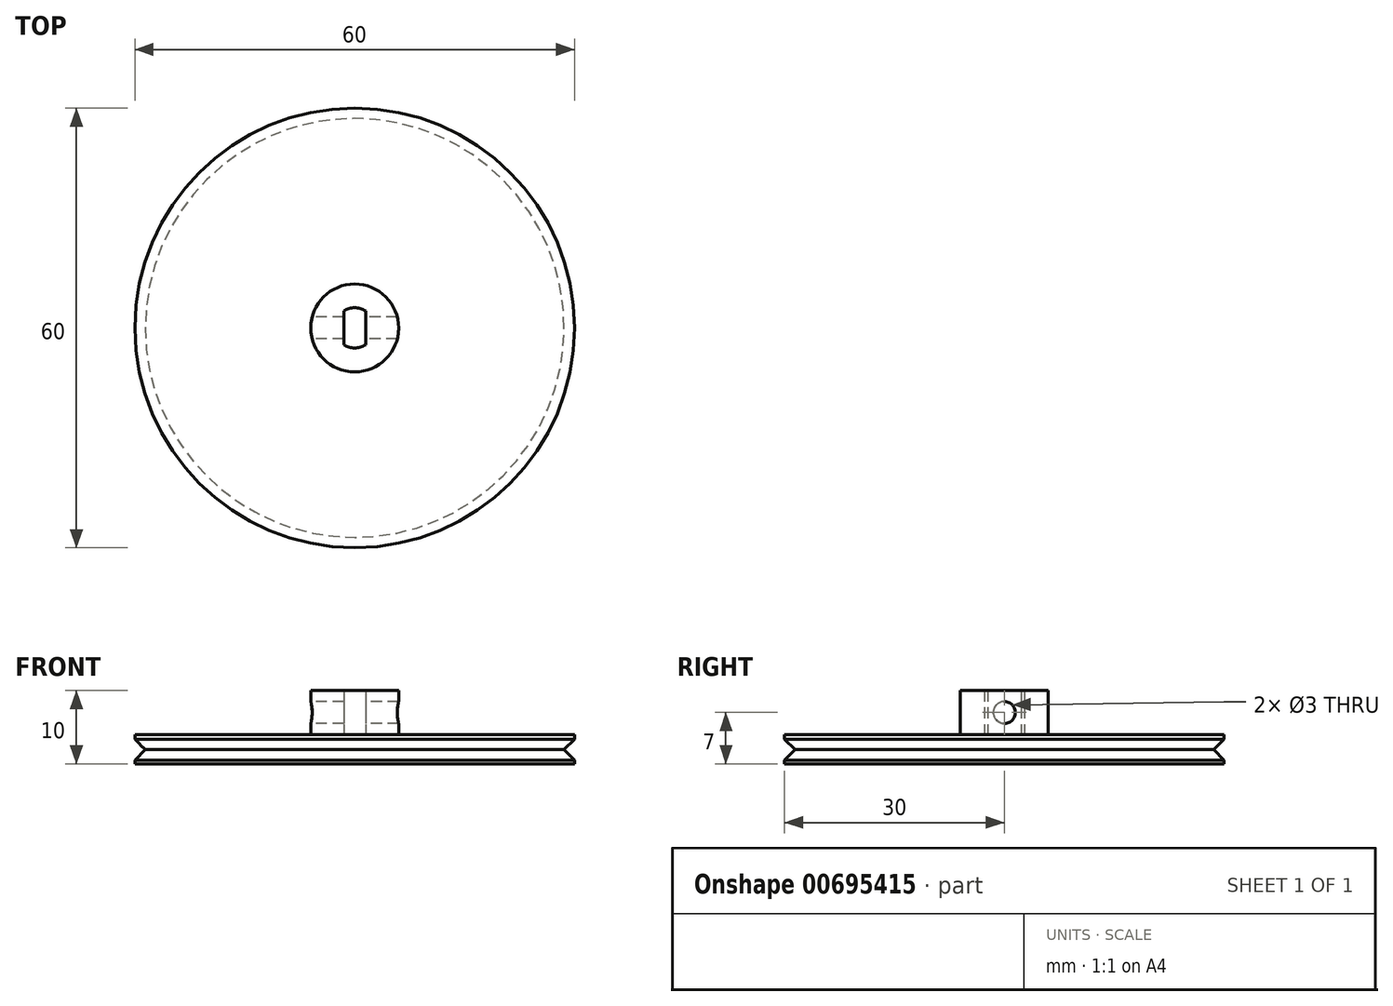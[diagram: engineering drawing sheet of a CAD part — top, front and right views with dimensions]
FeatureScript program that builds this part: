
annotation { "Feature Type Name" : "Feature", "Feature Type Description" : "" }
export const myFeature = defineFeature(function(context is Context, id is Id, definition is map)
    precondition{}
    {
        {
            var Q0;
            Q0=qCreatedBy(makeId("Top.planeOp"),FACE);
            var sketch = newSketch(context, id + "F0", { "sketchPlane" : qUnion([Q0])});
            skCircle(sketch, "E0", {"center": v(0, 0) * mm, "radius": 30 * mm});
            skSolve(sketch);
        }
        {
            var Q0;
            Q0=makeQuery(id+"F0.imprint","IMPRINT",FACE,{"disambiguationData":[TD([[makeQuery(id+"F0.imprint","IMPRINT",EDGE,{"derivedFrom":sQuery(id+"F0.wireOp",EDGE,"E0")}),1.0]])]});
            extrude(context, id + "F1", {"entities" : qUnion([Q0]), "depth" : 4 * mm, "offsetDistance" : 25 * mm});
        }
        {
            var Q0;
            Q0=makeQuery(id+"F1.opExtrude","CAP_FACE",FACE,{"disambiguationData":[OSD([sQuery(id+"F0.wireOp",EDGE,"E0")])],"isStart":false});
            var sketch = newSketch(context, id + "F2", { "sketchPlane" : qUnion([Q0])});
            skCircle(sketch, "E1", {"center": v(0, 0) * mm, "radius": 6 * mm});
            skLineSegment(sketch, "E2.bottom", {"start": v(1.5, -2.3) * mm, "end": v(-1.5, -2.3) * mm});
            skLineSegment(sketch, "E2.top", {"start": v(1.5, 2.3) * mm, "end": v(-1.5, 2.3) * mm});
            skLineSegment(sketch, "E2.left", {"start": v(1.5, -2.3) * mm, "end": v(1.5, 2.3) * mm});
            skLineSegment(sketch, "E2.right", {"start": v(-1.5, -2.3) * mm, "end": v(-1.5, 2.3) * mm});
            skArc(sketch, "E3", {"start": v(1.5, 2.3) * mm, "mid": v(0, 2.75) * mm, "end": v(-1.5, 2.3) * mm});
            skArc(sketch, "E4", {"start": v(-1.5, -2.3) * mm, "mid": v(0, -2.75) * mm, "end": v(1.5, -2.3) * mm});
            skSolve(sketch);
        }
        {
            var Q0;
            Q0=makeQuery(id+"F2.imprint","IMPRINT",FACE,{"disambiguationData":[TD([[makeQuery(id+"F2.imprint","IMPRINT",EDGE,{"derivedFrom":sQuery(id+"F2.wireOp",EDGE,"E1")}),1.0]])]});
            extrude(context, id + "F3", {"entities" : qUnion([Q0]), "operationType" : NewBodyOperationType.ADD, "depth" : 6 * mm, "offsetDistance" : 25 * mm});
        }
        {
            var Q0;
            Q0=qCreatedBy(makeId("Right.planeOp"),FACE);
            var sketch = newSketch(context, id + "F4", { "sketchPlane" : qUnion([Q0])});
            skCircle(sketch, "E5", {"center": v(0, 7) * mm, "radius": 1.5 * mm});
            skSolve(sketch);
        }
        {
            var Q0;
            Q0 = qSketchRegion(id + "F4", true);
            extrude(context, id + "F5", {"entities" : qUnion([Q0]), "operationType" : NewBodyOperationType.REMOVE, "endBound" : BoundingType.SYMMETRIC, "depth" : 24.6 * mm, "offsetDistance" : 25 * mm});
        }
        {
            var Q0;
            Q0=qCreatedBy(makeId("Front.planeOp"),FACE);
            var sketch = newSketch(context, id + "F6", { "sketchPlane" : qUnion([Q0])});
            skLineSegment(sketch, "E6", {"start": v(-30, 0) * mm, "end": v(-30, 4) * mm});
            skLineSegment(sketch, "E7", {"start": v(-30, 3.34) * mm, "end": v(-28.59, 1.93) * mm});
            skLineSegment(sketch, "E8", {"start": v(-28.59, 1.93) * mm, "end": v(-30, 0.51) * mm});
            skLineSegment(sketch, "E9", {"start": v(0, 22.53) * mm, "end": v(0, -10.3) * mm, "construction": true});
            skSolve(sketch);
        }
        {
            var Q0;
            Q0 = qSketchRegion(id + "F6", true);
            var Q1;
            Q1=sQuery(id+"F6.wireOp",EDGE,"E9");
            revolve(context, id + "F7", {"operationType" : NewBodyOperationType.REMOVE, "surfaceOperationType" : NewSurfaceOperationType.NEW, "entities" : qUnion([Q0]), "axis" : qUnion([Q1]), "revolveType" : RevolveType.FULL, "oppositeDirection" : true});
        }
    });
